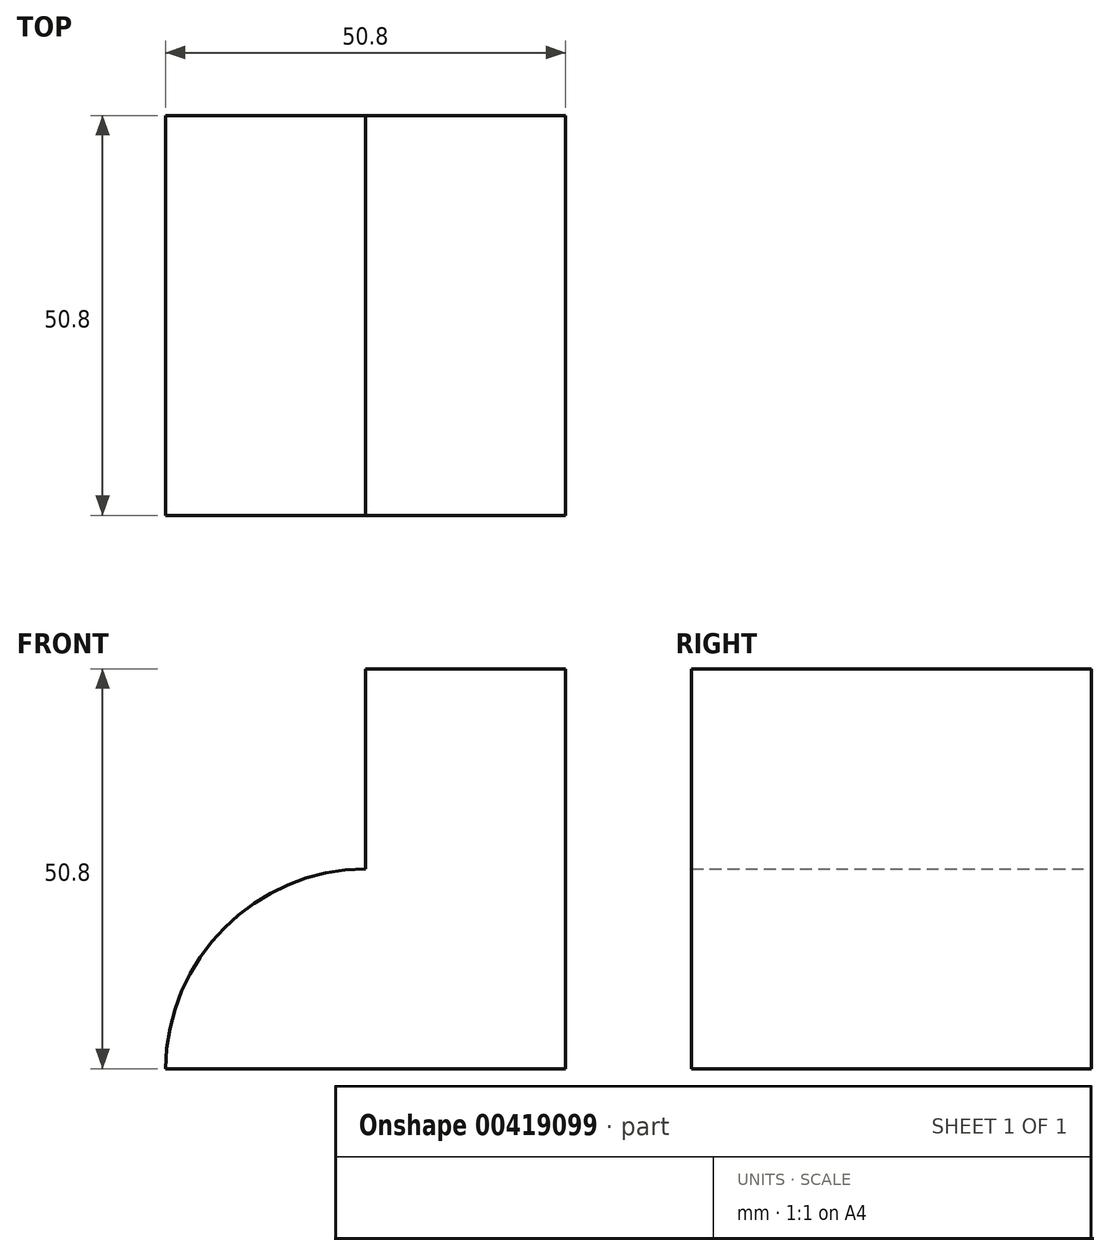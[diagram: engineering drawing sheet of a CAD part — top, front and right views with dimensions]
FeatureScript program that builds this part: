
annotation { "Feature Type Name" : "Feature", "Feature Type Description" : "" }
export const myFeature = defineFeature(function(context is Context, id is Id, definition is map)
    precondition{}
    {
        {
            var Q0;
            Q0=qCreatedBy(makeId("Front.planeOp"),FACE);
            var sketch = newSketch(context, id + "F0", { "sketchPlane" : qUnion([Q0])});
            skLineSegment(sketch, "E0", {"start": v(0, 0) * mm, "end": v(-50.8, 0) * mm});
            skLineSegment(sketch, "E1", {"start": v(0, 0) * mm, "end": v(0, 50.8) * mm});
            skLineSegment(sketch, "E2", {"start": v(0, 50.8) * mm, "end": v(-25.4, 50.8) * mm});
            skLineSegment(sketch, "E3", {"start": v(-25.4, 50.8) * mm, "end": v(-25.4, 25.4) * mm});
            skArc(sketch, "E4", {"start": v(-25.4, 25.4) * mm, "mid": v(-43.3, 17.9) * mm, "end": v(-50.8, 0) * mm});
            skSolve(sketch);
        }
        {
            var Q0;
            Q0 = qSketchRegion(id + "F0", true);
            extrude(context, id + "F1", {"entities" : qUnion([Q0]), "depth" : 50.8 * mm});
        }
    });
